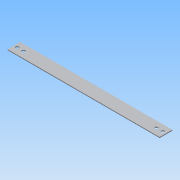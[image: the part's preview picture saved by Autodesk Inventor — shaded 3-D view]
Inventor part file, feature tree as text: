
AUTODESK INVENTOR PART (.ipt)
format: ipt  version: 2014 (Build 180170000, 170)  size: 86,528 bytes
history: native  units: in
note: dims shown in document units (in); Inventor stores cm internally (conversion verified against a paired STEP export)
features: extrude x2, sketch x2
ambient origin geometry x8: Origin, YZ Plane, XZ Plane, XY Plane, X Axis, Y Axis, Z Axis, Center Point
bodies: Solid1 (feature_tree)
feature tree (4):
  extrude  "Extrusion1"  Depth=12.0in
  extrude  "Extrusion2"  Depth=1.0in
  sketch  "Sketch2"  dims[d0=1.0in d1=12.0in]
  sketch  "Sketch3"  dims[d2=0.0625in d3=0.0in d4=0.25in d5=0.25in d6=0.5in d7=1.0in d8=0.0in]
